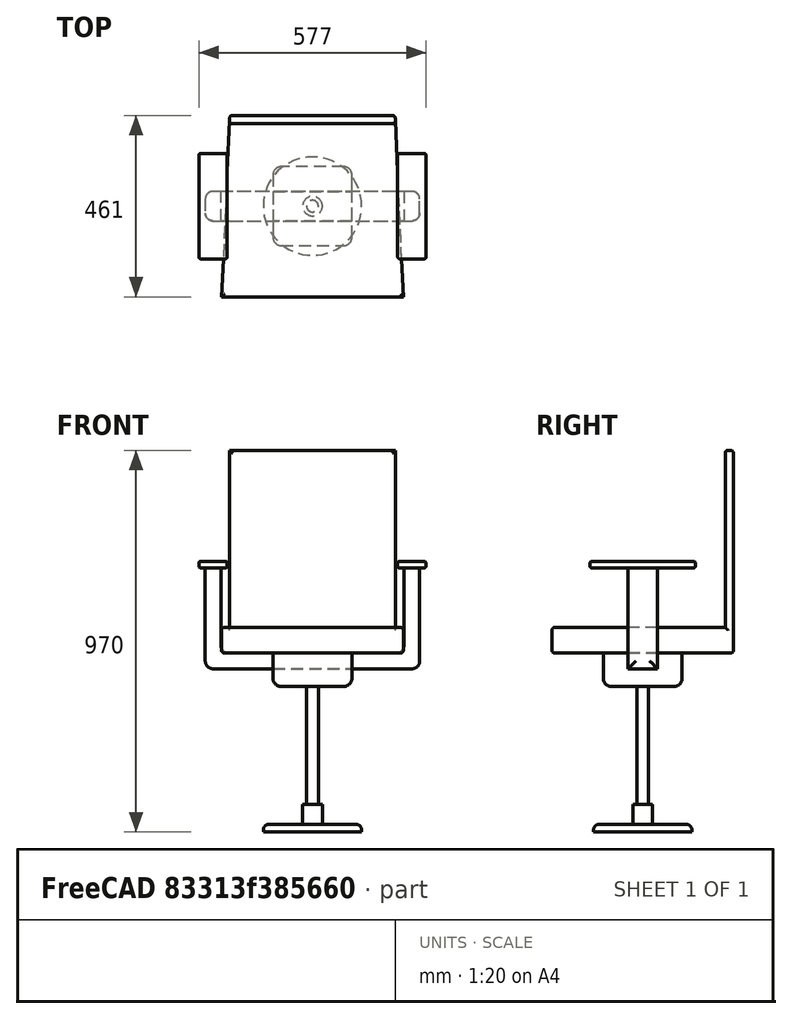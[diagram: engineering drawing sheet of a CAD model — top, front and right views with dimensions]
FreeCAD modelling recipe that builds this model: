
FCSTD DOCUMENT  (FreeCAD 1.0R39109 (Git))
Label: chair02_006
License: All rights reserved
LicenseURL: https://en.wikipedia.org/wiki/All_rights_reserved
objects: TechDraw::DrawViewBalloon×34, Sketcher::SketchObject×10, PartDesign::Pad×10, PartDesign::Fillet×7, PartDesign::Body×5, PartDesign::ShapeBinder×4, TechDraw::DrawSVGTemplate×4, TechDraw::DrawProjGroupItem×4, TechDraw::DrawPage×4, TechDraw::DrawViewDetail×3, TechDraw::DrawViewSection×2, App::Part×1
note: 80 computed .brp shape members not serialized (recipe doc carries the construction recipe); baked Part::Feature solids carry a one-line shape summary decoded from their .brp

FEATURE [Sketcher::SketchObject] Sketch
  ArcFitTolerance = 1e-06
  AttachmentSupport = -> [XY_Plane]
  FullyConstrained = true
  MakeInternals = false
  MapMode = 5
  sketch-geometry (1):
    g0: Circle CenterX=0 CenterY=0 CenterZ=0 NormalX=0 NormalY=0 NormalZ=1 AngleXU=0 Radius=125
  constraints (2):
    c: Diameter(g0) = 250
    c: Coincident(g0,g-1)
FEATURE [PartDesign::Pad] Pad
  Direction = (0,0,1)
  Length = 20
  Length2 = 10
  Profile = -> Sketch
  ReferenceAxis = -> Sketch [N_Axis]
  Refine = true
  Suppressed = false
  Type = 0
FEATURE [Sketcher::SketchObject] Sketch001
  ArcFitTolerance = 1e-06
  AttachmentSupport = -> [Pad]
  FullyConstrained = true
  MakeInternals = false
  MapMode = 5
  Placement = pos=(0,0,20) rot=(0,0,1;0rad)
  sketch-geometry (1):
    g0: Circle CenterX=0 CenterY=0 CenterZ=0 NormalX=0 NormalY=0 NormalZ=1 AngleXU=0 Radius=25
  constraints (2):
    c: Diameter(g0) = 50
    c: Coincident(g0,g-1)
FEATURE [PartDesign::Pad] Pad001
  BaseFeature = -> Pad
  Direction = (0,0,1)
  Length = 50
  Length2 = 10
  Profile = -> Sketch001
  ReferenceAxis = -> Sketch001 [N_Axis]
  Refine = true
  Suppressed = false
  Type = 0
FEATURE [PartDesign::ShapeBinder] CopyPad001  label="Body2_Sketch_P.lane"
  Placement = pos=(0,0,50) rot=(0,0,1;0rad)
  TraceSupport = false
FEATURE [Sketcher::SketchObject] Sketch002
  ArcFitTolerance = 1e-06
  AttachmentSupport = -> [CopyPad001]
  FullyConstrained = true
  MakeInternals = false
  MapMode = 5
  Placement = pos=(0,0,70) rot=(0,0,1;0rad)
  sketch-geometry (1):
    g0: Circle CenterX=0 CenterY=0 CenterZ=0 NormalX=0 NormalY=0 NormalZ=1 AngleXU=0 Radius=15
  constraints (2):
    c: Diameter(g0) = 30
    c: Coincident(g0,g-1)
FEATURE [PartDesign::Pad] Pad002
  Direction = (0,0,1)
  Length = 300
  Length2 = 10
  Placement = pos=(0,0,50) rot=(0,0,1;0rad)
  Profile = -> Sketch002
  ReferenceAxis = -> Sketch002 [N_Axis]
  Refine = true
  Suppressed = false
  Type = 0
FEATURE [PartDesign::Body] Body001  label="Body2"
  AllowCompound = false
  Group = -> [CopyPad001,Sketch002,Pad002]
  Origin = -> Origin001
  Tip = -> Pad002
FEATURE [PartDesign::ShapeBinder] CopyPad002  label="Body3_Sketch_Plane"
  Placement = pos=(0,0,300) rot=(0,0,1;0rad)
  TraceSupport = false
FEATURE [Sketcher::SketchObject] Sketch003
  ArcFitTolerance = 1e-06
  AttachmentSupport = -> [CopyPad002]
  FullyConstrained = true
  MakeInternals = false
  MapMode = 5
  Placement = pos=(0,0,370) rot=(0,0,1;0rad)
  sketch-geometry (5):
    g0: LineSegment StartX=-100 StartY=-100 StartZ=0 EndX=100 EndY=-100 EndZ=0
    g1: LineSegment StartX=100 StartY=-100 StartZ=0 EndX=100 EndY=100 EndZ=0
    g2: LineSegment StartX=100 StartY=100 StartZ=0 EndX=-100 EndY=100 EndZ=0
    g3: LineSegment StartX=-100 StartY=100 StartZ=0 EndX=-100 EndY=-100 EndZ=0
    g4: GeomPoint [constr] X=0 Y=0 Z=0
  constraints (12):
    c: Coincident(g0,g1)
    c: Coincident(g1,g2)
    c: Coincident(g2,g3)
    c: Coincident(g3,g0)
    c: Horizontal(g0)
    c: Horizontal(g2)
    c: Vertical(g1)
    c: Vertical(g3)
    c: Symmetric(g2,g0,g4)
    c: Distance(g1,g3) = 200
    c: Distance(g0,g2) = 200
    c: Coincident(g4,g-1)
FEATURE [PartDesign::Pad] Pad003
  Direction = (0,0,1)
  Length = 45
  Length2 = 10
  Placement = pos=(0,0,300) rot=(0,0,1;0rad)
  Profile = -> Sketch003
  ReferenceAxis = -> Sketch003 [N_Axis]
  Refine = true
  Suppressed = false
  Type = 0
FEATURE [PartDesign::ShapeBinder] CopyPad003  label="Body4_Sketch_Plane"
  Placement = pos=(0,0,45) rot=(0,0,1;0rad)
  TraceSupport = false
FEATURE [Sketcher::SketchObject] Sketch004
  ArcFitTolerance = 1e-06
  AttachmentSupport = -> [CopyPad003]
  FullyConstrained = true
  MakeInternals = false
  MapMode = 5
  Placement = pos=(0,0,415) rot=(0,0,1;0rad)
  sketch-geometry (5):
    g0: LineSegment StartX=-272.5 StartY=-37.5 StartZ=0 EndX=272.5 EndY=-37.5 EndZ=0
    g1: LineSegment StartX=272.5 StartY=-37.5 StartZ=0 EndX=272.5 EndY=37.5 EndZ=0
    g2: LineSegment StartX=272.5 StartY=37.5 StartZ=0 EndX=-272.5 EndY=37.5 EndZ=0
    g3: LineSegment StartX=-272.5 StartY=37.5 StartZ=0 EndX=-272.5 EndY=-37.5 EndZ=0
    g4: GeomPoint [constr] X=0 Y=0 Z=0
  constraints (12):
    c: Coincident(g0,g1)
    c: Coincident(g1,g2)
    c: Coincident(g2,g3)
    c: Coincident(g3,g0)
    c: Horizontal(g0)
    c: Horizontal(g2)
    c: Vertical(g1)
    c: Vertical(g3)
    c: Symmetric(g2,g0,g4)
    c: Distance(g1,g3) = 545
    c: Distance(g0,g2) = 75
    c: Coincident(g4,g-1)
FEATURE [PartDesign::Pad] Pad004
  Direction = (0,0,1)
  Length = 40
  Length2 = 10
  Placement = pos=(0,0,45) rot=(0,0,1;0rad)
  Profile = -> Sketch004
  ReferenceAxis = -> Sketch004 [N_Axis]
  Refine = true
  Suppressed = false
  Type = 0
FEATURE [Sketcher::SketchObject] Sketch005
  ArcFitTolerance = 1e-06
  AttachmentSupport = -> [Pad004]
  ExternalGeometry = -> [Pad004]
  FullyConstrained = true
  MakeInternals = false
  MapMode = 5
  Placement = pos=(0,0,455) rot=(0,0,1;0rad)
  sketch-geometry (8):
    g0: LineSegment StartX=-272.5 StartY=37.5 StartZ=0 EndX=-272.5 EndY=-37.5 EndZ=0
    g1: LineSegment StartX=-272.5 StartY=-37.5 StartZ=0 EndX=-232.5 EndY=-37.5 EndZ=0
    g2: LineSegment StartX=-232.5 StartY=-37.5 StartZ=0 EndX=-232.5 EndY=37.5 EndZ=0
    g3: LineSegment StartX=-232.5 StartY=37.5 StartZ=0 EndX=-272.5 EndY=37.5 EndZ=0
    g4: LineSegment StartX=272.5 StartY=37.5 StartZ=0 EndX=232.5 EndY=37.5 EndZ=0
    g5: LineSegment StartX=232.5 StartY=37.5 StartZ=0 EndX=232.5 EndY=-37.5 EndZ=0
    g6: LineSegment StartX=232.5 StartY=-37.5 StartZ=0 EndX=272.5 EndY=-37.5 EndZ=0
    g7: LineSegment StartX=272.5 StartY=-37.5 StartZ=0 EndX=272.5 EndY=37.5 EndZ=0
  constraints (22):
    c: Coincident(g0,g1)
    c: Coincident(g1,g2)
    c: Coincident(g2,g3)
    c: Coincident(g3,g0)
    c: Vertical(g0)
    c: Vertical(g2)
    c: Horizontal(g1)
    c: Horizontal(g3)
    c: Coincident(g0,g-3)
    c: PointOnObject(g1,g-4)
    c: DistanceX(g3,g3) = 40
    c: Coincident(g4,g5)
    c: Coincident(g5,g6)
    c: Coincident(g6,g7)
    c: Coincident(g7,g4)
    c: Horizontal(g4)
    c: Horizontal(g6)
    c: Vertical(g5)
    c: Vertical(g7)
    c: Coincident(g4,g-3)
    c: PointOnObject(g5,g-4)
    c: Equal(g4,g3)
FEATURE [PartDesign::Pad] Pad005
  BaseFeature = -> Pad004
  Direction = (0,0,1)
  Length = 216
  Length2 = 10
  Placement = pos=(0,0,45) rot=(0,0,1;0rad)
  Profile = -> Sketch005
  ReferenceAxis = -> Sketch005 [N_Axis]
  Refine = true
  Suppressed = false
  Type = 0
FEATURE [Sketcher::SketchObject] Sketch006
  ArcFitTolerance = 1e-06
  AttachmentSupport = -> [Pad005]
  ExternalGeometry = -> [Pad005]
  FullyConstrained = true
  MakeInternals = false
  MapMode = 5
  Placement = pos=(0,0,671) rot=(0,0,1;0rad)
  sketch-geometry (16):
    g0: LineSegment StartX=-288.5 StartY=134 StartZ=0 EndX=-288.5 EndY=-134 EndZ=0
    g1: LineSegment StartX=-288.5 StartY=-134 StartZ=0 EndX=-216.5 EndY=-134 EndZ=0
    g2: LineSegment StartX=-216.5 StartY=-134 StartZ=0 EndX=-216.5 EndY=134 EndZ=0
    g3: LineSegment StartX=-216.5 StartY=134 StartZ=0 EndX=-288.5 EndY=134 EndZ=0
    g4: LineSegment StartX=216.5 StartY=134 StartZ=0 EndX=216.5 EndY=-134 EndZ=0
    g5: LineSegment StartX=216.5 StartY=-134 StartZ=0 EndX=288.5 EndY=-134 EndZ=0
    g6: LineSegment StartX=288.5 StartY=-134 StartZ=0 EndX=288.5 EndY=134 EndZ=0
    g7: LineSegment StartX=288.5 StartY=134 StartZ=0 EndX=216.5 EndY=134 EndZ=0
    g8: LineSegment [constr] StartX=-272.5 StartY=37.5 StartZ=0 EndX=-232.5 EndY=-37.5 EndZ=0
    g9: LineSegment [constr] StartX=-252.5 StartY=0 StartZ=0 EndX=-272.5 EndY=-37.5 EndZ=0
    g10: LineSegment [constr] StartX=232.5 StartY=37.5 StartZ=0 EndX=272.5 EndY=-37.5 EndZ=0
    g11: LineSegment [constr] StartX=272.5 StartY=37.5 StartZ=0 EndX=252.5 EndY=0 EndZ=0
    g12: LineSegment [constr] StartX=-216.5 StartY=134 StartZ=0 EndX=-288.5 EndY=-134 EndZ=0
    g13: LineSegment [constr] StartX=-288.5 StartY=134 StartZ=0 EndX=-252.5 EndY=0 EndZ=0
    g14: LineSegment [constr] StartX=216.5 StartY=134 StartZ=0 EndX=288.5 EndY=-134 EndZ=0
    g15: LineSegment [constr] StartX=288.5 StartY=134 StartZ=0 EndX=252.5 EndY=0 EndZ=0
  constraints (38):
    c: Coincident(g0,g1)
    c: Coincident(g1,g2)
    c: Coincident(g2,g3)
    c: Coincident(g3,g0)
    c: Vertical(g0)
    c: Vertical(g2)
    c: Horizontal(g1)
    c: Horizontal(g3)
    c: Coincident(g4,g5)
    c: Coincident(g5,g6)
    c: Coincident(g6,g7)
    c: Coincident(g7,g4)
    c: Vertical(g4)
    c: Vertical(g6)
    c: Horizontal(g5)
    c: Horizontal(g7)
    c: Equal(g7,g3)
    c: Equal(g2,g4)
    c: DistanceX(g3,g3) = 72
    c: Coincident(g8,g-4)
    c: Coincident(g8,g-3)
    c: Coincident(g9,g-4)
    c: Coincident(g10,g-5)
    c: Coincident(g10,g-6)
    c: Coincident(g11,g-6)
    c: Symmetric(g10,g10,g11)
    c: Symmetric(g8,g8,g9)
    c: Coincident(g12,g2)
    c: Coincident(g12,g0)
    c: Coincident(g13,g0)
    c: Symmetric(g12,g12,g13)
    c: Coincident(g9,g13)
    c: Coincident(g14,g4)
    c: Coincident(g14,g5)
    c: Coincident(g15,g6)
    c: Symmetric(g14,g14,g15)
    c: Coincident(g15,g11)
    c: DistanceY(g2,g2) = 268
FEATURE [PartDesign::Pad] Pad006
  BaseFeature = -> Pad005
  Direction = (0,0,1)
  Length = 17
  Length2 = 10
  Placement = pos=(0,0,45) rot=(0,0,1;0rad)
  Profile = -> Sketch006
  ReferenceAxis = -> Sketch006 [N_Axis]
  Refine = true
  Suppressed = false
  Type = 0
FEATURE [PartDesign::ShapeBinder] CopyPad006  label="Body5_Sketch_Plane"
  Placement = pos=(0,0,45) rot=(0,0,1;0rad)
  TraceSupport = false
FEATURE [Sketcher::SketchObject] Sketch009
  ArcFitTolerance = 1e-06
  AttachmentSupport = -> [Pad003]
  ExternalGeometry = -> [Pad003]
  FullyConstrained = true
  MakeInternals = false
  MapMode = 5
  Placement = pos=(0,0,415) rot=(0,0,1;0rad)
  sketch-geometry (8):
    g0: LineSegment StartX=-100 StartY=100 StartZ=0 EndX=-100 EndY=37.5 EndZ=0
    g1: LineSegment StartX=-100 StartY=37.5 StartZ=0 EndX=100 EndY=37.5 EndZ=0
    g2: LineSegment StartX=100 StartY=37.5 StartZ=0 EndX=100 EndY=100 EndZ=0
    g3: LineSegment StartX=100 StartY=100 StartZ=0 EndX=-100 EndY=100 EndZ=0
    g4: LineSegment StartX=100 StartY=-100 StartZ=0 EndX=100 EndY=-37.5 EndZ=0
    g5: LineSegment StartX=100 StartY=-37.5 StartZ=0 EndX=-100 EndY=-37.5 EndZ=0
    g6: LineSegment StartX=-100 StartY=-37.5 StartZ=0 EndX=-100 EndY=-100 EndZ=0
    g7: LineSegment StartX=-100 StartY=-100 StartZ=0 EndX=100 EndY=-100 EndZ=0
  constraints (21):
    c: Coincident(g0,g1)
    c: Coincident(g1,g2)
    c: Coincident(g2,g3)
    c: Coincident(g3,g0)
    c: Vertical(g0)
    c: Vertical(g2)
    c: Horizontal(g1)
    c: Horizontal(g3)
    c: Coincident(g0,g-3)
    c: PointOnObject(g1,g-4)
    c: Coincident(g4,g5)
    c: Coincident(g5,g6)
    c: Coincident(g6,g7)
    c: Coincident(g7,g4)
    c: Vertical(g6)
    c: Horizontal(g5)
    c: Horizontal(g7)
    c: Coincident(g4,g-4)
    c: PointOnObject(g5,g-3)
    c: DistanceY(g4,g1) = 75
    c: Symmetric(g1,g4,g-1)
FEATURE [PartDesign::Pad] Pad009
  BaseFeature = -> Pad003
  Direction = (0,0,1)
  Length = 40
  Length2 = 10
  Placement = pos=(0,0,300) rot=(0,0,1;0rad)
  Profile = -> Sketch009
  ReferenceAxis = -> Sketch009 [N_Axis]
  Refine = true
  Suppressed = false
  Type = 0
FEATURE [PartDesign::Fillet] Fillet003
  Base = -> Pad006 [Edge43,Edge48,Edge35,Edge40,Edge39,Edge37,Edge45,Edge47,Edge34,Edge38,Edge36,Edge33,Edge24,Edge22,Edge23,Edge21,Edge29,Edge31,Edge42,Edge46,Edge44,Edge32,Edge30,Edge41]
  BaseFeature = -> Pad006
  Placement = pos=(0,0,45) rot=(0,0,1;0rad)
  Radius = 5
  Refine = true
  SupportTransform = false
  Suppressed = false
  UseAllEdges = false
FEATURE [PartDesign::Fillet] Fillet004
  Base = -> Fillet003 [Edge57,Edge58,Edge36,Edge28,Edge22,Edge29,Edge27,Edge31]
  BaseFeature = -> Fillet003
  Placement = pos=(0,0,45) rot=(0,0,1;0rad)
  Radius = 20
  Refine = true
  SupportTransform = false
  Suppressed = false
  UseAllEdges = false
FEATURE [PartDesign::Body] Body003  label="Body4"
  AllowCompound = false
  Group = -> [CopyPad003,Sketch004,Pad004,Sketch005,Pad005,Sketch006,Pad006,Fillet003,Fillet004]
  Origin = -> Origin003
  Tip = -> Fillet004
FEATURE [PartDesign::Fillet] Fillet005
  Base = -> Pad009 [Edge7,Edge5,Edge24,Edge23,Edge1,Edge2,Edge4,Edge3]
  BaseFeature = -> Pad009
  Placement = pos=(0,0,300) rot=(0,0,1;0rad)
  Radius = 20
  Refine = true
  SupportTransform = false
  Suppressed = false
  UseAllEdges = false
FEATURE [PartDesign::Body] Body002  label="Body3"
  AllowCompound = false
  Group = -> [CopyPad002,Sketch003,Pad003,Sketch009,Pad009,Fillet005]
  Origin = -> Origin002
  Tip = -> Fillet005
FEATURE [PartDesign::Fillet] Fillet006
  Base = -> Pad001 [Edge3]
  BaseFeature = -> Pad001
  Radius = 15
  Refine = true
  SupportTransform = false
  Suppressed = false
  UseAllEdges = false
FEATURE [PartDesign::Body] Body  label="Body1"
  AllowCompound = false
  Group = -> [Sketch,Pad,Sketch001,Pad001,Fillet006]
  Origin = -> Origin
  Tip = -> Fillet006
FEATURE [Sketcher::SketchObject] Sketch007
  ArcFitTolerance = 1e-06
  AttachmentSupport = -> [CopyPad006]
  FullyConstrained = true
  MakeInternals = false
  MapMode = 5
  Placement = pos=(0,0,455) rot=(0,0,1;0rad)
  sketch-geometry (8):
    g0: LineSegment StartX=-210 StartY=230.5 StartZ=0 EndX=-231 EndY=-230.5 EndZ=0
    g1: LineSegment StartX=-231 StartY=-230.5 StartZ=0 EndX=231 EndY=-230.5 EndZ=0
    g2: LineSegment StartX=231 StartY=-230.5 StartZ=0 EndX=210 EndY=230.5 EndZ=0
    g3: LineSegment StartX=210 StartY=230.5 StartZ=0 EndX=-210 EndY=230.5 EndZ=0
    g4: LineSegment [constr] StartX=210 StartY=230.5 StartZ=0 EndX=2.84e-14 EndY=0 EndZ=0
    g5: LineSegment [constr] StartX=2.84e-14 StartY=0 StartZ=0 EndX=-210 EndY=230.5 EndZ=0
    g6: LineSegment [constr] StartX=210 StartY=230.5 StartZ=0 EndX=210 EndY=0 EndZ=0
    g7: LineSegment [constr] StartX=231 StartY=-230.5 StartZ=0 EndX=231 EndY=0 EndZ=0
  constraints (20):
    c: Coincident(g2,g1)
    c: DistanceX(g1,g1) = 462
    c: DistanceX(g3,g3) = 420
    c: Coincident(g1,g0)
    c: Symmetric(g2,g0,g-2)
    c: Coincident(g2,g3)
    c: Coincident(g3,g0)
    c: Coincident(g4,g2)
    c: Coincident(g4,g-1)
    c: Coincident(g5,g4)
    c: Coincident(g5,g0)
    c: DistanceY(g2,g2) = 461
    c: Coincident(g6,g2)
    c: PointOnObject(g6,g-1)
    c: Vertical(g6)
    c: Coincident(g7,g1)
    c: PointOnObject(g7,g-1)
    c: Vertical(g7)
    c: Equal(g7,g6)
    c: Symmetric(g1,g0,g-2)
FEATURE [PartDesign::Pad] Pad007
  Direction = (0,0,1)
  Length = 65
  Length2 = 10
  Placement = pos=(0,0,45) rot=(0,0,1;0rad)
  Profile = -> Sketch007
  ReferenceAxis = -> Sketch007 [N_Axis]
  Refine = true
  Suppressed = false
  Type = 0
FEATURE [Sketcher::SketchObject] Sketch008
  ArcFitTolerance = 1e-06
  AttachmentSupport = -> [Pad007]
  ExternalGeometry = -> [Pad007]
  FullyConstrained = true
  MakeInternals = false
  MapMode = 5
  Placement = pos=(0,0,520) rot=(0,0,1;0rad)
  sketch-geometry (4):
    g0: LineSegment StartX=-210 StartY=230.5 StartZ=0 EndX=210 EndY=230.5 EndZ=0
    g1: LineSegment StartX=-210 StartY=230.5 StartZ=0 EndX=-210.957 EndY=209.5 EndZ=0
    g2: LineSegment StartX=-210.957 StartY=209.5 StartZ=0 EndX=210.957 EndY=209.5 EndZ=0
    g3: LineSegment StartX=210 StartY=230.5 StartZ=0 EndX=210.957 EndY=209.5 EndZ=0
  constraints (10):
    c: Coincident(g0,g-3)
    c: Coincident(g0,g-4)
    c: Coincident(g1,g0)
    c: PointOnObject(g1,g-3)
    c: Coincident(g2,g1)
    c: PointOnObject(g2,g-4)
    c: Horizontal(g2)
    c: Coincident(g3,g0)
    c: Coincident(g3,g2)
    c: DistanceY(g1,g1) = 21
FEATURE [PartDesign::Pad] Pad008
  BaseFeature = -> Pad007
  Direction = (0,0,1)
  Length = 450
  Length2 = 10
  Placement = pos=(0,0,45) rot=(0,0,1;0rad)
  Profile = -> Sketch008
  ReferenceAxis = -> Sketch008 [N_Axis]
  Refine = true
  Suppressed = false
  Type = 0
FEATURE [PartDesign::Fillet] Fillet
  Base = -> Pad008 [Edge13,Edge14,Edge17,Edge18,Edge12,Edge11]
  BaseFeature = -> Pad008
  Placement = pos=(0,0,45) rot=(0,0,1;0rad)
  Radius = 7
  Refine = true
  SupportTransform = false
  Suppressed = false
  UseAllEdges = false
FEATURE [PartDesign::Fillet] Fillet001
  Base = -> Fillet [Edge10,Edge17,Edge22]
  BaseFeature = -> Fillet
  Placement = pos=(0,0,45) rot=(0,0,1;0rad)
  Radius = 7
  Refine = true
  SupportTransform = false
  Suppressed = false
  UseAllEdges = false
FEATURE [PartDesign::Fillet] Fillet002
  Base = -> Fillet001 [Edge13,Edge9,Edge3,Edge12]
  BaseFeature = -> Fillet001
  Placement = pos=(0,0,45) rot=(0,0,1;0rad)
  Radius = 7
  Refine = true
  SupportTransform = false
  Suppressed = false
  UseAllEdges = false
FEATURE [PartDesign::Body] Body004  label="Body5"
  AllowCompound = false
  Group = -> [CopyPad006,Sketch007,Pad007,Sketch008,Pad008,Fillet,Fillet001,Fillet002]
  Origin = -> Origin004
  Tip = -> Fillet002
FEATURE [App::Part] Part  label="chair02"
  Group = -> [Body,Body001,Body002,Body003,Body004]
  Origin = -> Origin005
FEATURE [TechDraw::DrawSVGTemplate] Template  label="テンプレート"
  Height = 210
  Orientation = 1
  Template = <userpath>/AppData/Local/Programs/FreeCAD 1.0/data/Mod/TechDraw/Templates/A4_Landscape_blank.svg
  Width = 297
FEATURE [TechDraw::DrawProjGroupItem] View
  CoarseView = false
  Direction = (0,0,1)
  Focus = 100
  HardHidden = true
  IsoCount = 0
  IsoHidden = false
  IsoVisible = false
  LockPosition = false
  Perspective = false
  Rotation = 0
  RotationVector = (1,0,0)
  Scale = 0.333333
  ScaleType = 2
  ScrubCount = 1
  SeamHidden = false
  SeamVisible = false
  SmoothHidden = false
  SmoothVisible = true
  Source = -> [Part]
  Type = 0
  X = 148.5
  XDirection = (1,0,0)
  Y = 105
FEATURE [TechDraw::DrawViewBalloon] Balloon  label="吹き出し"
  BubbleShape = 1
  EndType = 0
  EndTypeScale = 1
  KinkLength = 5
  LockPosition = false
  OriginX = 208.147
  OriginY = 228.561
  Rotation = 0
  Scale = 0.2
  ScaleType = 2
  ShapeScale = 1
  SourceView = -> View
  Text = R7
  TextWrapLen = -1
  X = 254.043
  Y = 271.744
FEATURE [TechDraw::DrawViewBalloon] Balloon001  label="吹き出し001"
  BubbleShape = 1
  EndType = 0
  EndTypeScale = 1
  KinkLength = 5
  LockPosition = false
  OriginX = 208.8
  OriginY = 211.781
  Rotation = 0
  Scale = 0.2
  ScaleType = 2
  ShapeScale = 1
  SourceView = -> View
  Text = R7
  TextWrapLen = -1
  X = 266.359
  Y = 184.985
FEATURE [TechDraw::DrawViewBalloon] Balloon002  label="吹き出し002"
  BubbleShape = 1
  EndType = 0
  EndTypeScale = 1
  KinkLength = 5
  LockPosition = false
  OriginX = -208.147
  OriginY = 228.561
  Rotation = 0
  Scale = 0.2
  ScaleType = 2
  ShapeScale = 1
  SourceView = -> View
  Text = R7
  TextWrapLen = -1
  X = -260.711
  Y = 284.764
FEATURE [TechDraw::DrawViewBalloon] Balloon003  label="吹き出し003"
  BubbleShape = 1
  EndType = 0
  EndTypeScale = 1
  KinkLength = 5
  LockPosition = false
  OriginX = -208.439
  OriginY = 210.657
  Rotation = 0
  Scale = 0.2
  ScaleType = 2
  ShapeScale = 1
  SourceView = -> View
  Text = R7
  TextWrapLen = -1
  X = -265.342
  Y = 208.001
FEATURE [TechDraw::DrawViewBalloon] Balloon004  label="吹き出し004"
  BubbleShape = 1
  EndType = 0
  EndTypeScale = 1
  KinkLength = 5
  LockPosition = false
  OriginX = 287.036
  OriginY = 132.536
  Rotation = 0
  Scale = 0.2
  ScaleType = 2
  ShapeScale = 1
  SourceView = -> View
  Text = R5
  TextWrapLen = -1
  X = 347.036
  Y = 192.536
FEATURE [TechDraw::DrawViewBalloon] Balloon005  label="吹き出し005"
  BubbleShape = 1
  EndType = 0
  EndTypeScale = 1
  KinkLength = 5
  LockPosition = false
  OriginX = 217.209
  OriginY = 132.437
  Rotation = 0
  Scale = 0.2
  ScaleType = 2
  ShapeScale = 1
  SourceView = -> View
  Text = R5
  TextWrapLen = -1
  X = 158.961
  Y = 163.416
FEATURE [TechDraw::DrawViewBalloon] Balloon006  label="吹き出し006"
  BubbleShape = 1
  EndType = 0
  EndTypeScale = 1
  KinkLength = 5
  LockPosition = false
  OriginX = 287.036
  OriginY = -132.536
  Rotation = 0
  Scale = 0.2
  ScaleType = 2
  ShapeScale = 1
  SourceView = -> View
  Text = R5
  TextWrapLen = -1
  X = 345.184
  Y = -173.752
FEATURE [TechDraw::DrawViewBalloon] Balloon007  label="吹き出し007"
  BubbleShape = 1
  EndType = 0
  EndTypeScale = 1
  KinkLength = 5
  LockPosition = false
  OriginX = 217.101
  OriginY = -132.016
  Rotation = 0
  Scale = 0.2
  ScaleType = 2
  ShapeScale = 1
  SourceView = -> View
  Text = R5
  TextWrapLen = -1
  X = 162.924
  Y = -168.913
FEATURE [TechDraw::DrawPage] Page  label="用紙"
  KeepUpdated = true
  NextBalloonIndex = 11
  ProjectionType = 0
  Template = -> Template
  Views = -> [View,Balloon,Balloon001,Balloon002,Balloon003,Balloon004,Balloon005,Balloon006,Balloon007]
FEATURE [TechDraw::DrawSVGTemplate] Template001  label="テンプレート001"
  Height = 210
  Orientation = 1
  Template = <userpath>/AppData/Local/Programs/FreeCAD 1.0/data/Mod/TechDraw/Templates/A4_Landscape_blank.svg
  Width = 297
FEATURE [TechDraw::DrawProjGroupItem] View001
  CoarseView = false
  Direction = (0,-1,0)
  Focus = 100
  HardHidden = true
  IsoCount = 0
  IsoHidden = false
  IsoVisible = false
  LockPosition = false
  Perspective = false
  Rotation = 0
  RotationVector = (1,0,0)
  Scale = 0.2
  ScaleType = 2
  ScrubCount = 1
  SeamHidden = false
  SeamVisible = false
  SmoothHidden = false
  SmoothVisible = true
  Source = -> [Part]
  Type = 0
  X = 77.6951
  XDirection = (1,0,0)
  Y = 106.438
FEATURE [TechDraw::DrawViewDetail] Detail  label="詳細"
  AnchorPoint = (251.74,189.44,0)
  BaseView = -> View001
  CoarseView = false
  Direction = (0,-1,0)
  Focus = 100
  HardHidden = true
  IsoCount = 0
  IsoHidden = false
  IsoVisible = false
  LockPosition = false
  Perspective = false
  Radius = 39
  Reference = 1
  Rotation = 0
  Scale = 0.7
  ScaleType = 2
  ScrubCount = 1
  SeamHidden = false
  SeamVisible = false
  ShowHighlight = true
  ShowMatting = true
  SmoothHidden = false
  SmoothVisible = true
  Source = -> [Part]
  X = 198.751
  XDirection = (1,0,0)
  Y = 153.271
FEATURE [TechDraw::DrawViewDetail] Detail001  label="詳細001"
  AnchorPoint = (225.2,3.67,0)
  BaseView = -> View001
  CoarseView = false
  Direction = (0,-1,0)
  Focus = 100
  HardHidden = true
  IsoCount = 0
  IsoHidden = false
  IsoVisible = false
  LockPosition = false
  Perspective = false
  Radius = 42
  Reference = 1
  Rotation = 0
  Scale = 0.7
  ScaleType = 2
  ScrubCount = 1
  SeamHidden = false
  SeamVisible = false
  ShowHighlight = true
  ShowMatting = true
  SmoothHidden = false
  SmoothVisible = true
  Source = -> [Part]
  X = 202.09
  XDirection = (1,0,0)
  Y = 54.0888
FEATURE [TechDraw::DrawViewBalloon] Balloon008  label="吹き出し008"
  BubbleShape = 1
  EndType = 0
  EndTypeScale = 1
  KinkLength = 5
  LockPosition = false
  OriginX = 3.59213
  OriginY = 29.3328
  Rotation = 0
  Scale = 0.2
  ScaleType = 2
  ShapeScale = 1
  SourceView = -> Detail001
  Text = R7
  TextWrapLen = -1
  X = 41.6562
  Y = 43.3944
FEATURE [TechDraw::DrawViewBalloon] Balloon009  label="吹き出し009"
  BubbleShape = 1
  EndType = 0
  EndTypeScale = 1
  KinkLength = 5
  LockPosition = false
  OriginX = 3.484
  OriginY = -31.9238
  Rotation = 0
  Scale = 0.2
  ScaleType = 2
  ShapeScale = 1
  SourceView = -> Detail001
  Text = R7
  TextWrapLen = -1
  X = 41.6149
  Y = -49.4301
FEATURE [TechDraw::DrawViewBalloon] Balloon012  label="吹き出し012"
  BubbleShape = 1
  EndType = 0
  EndTypeScale = 1
  KinkLength = 5
  LockPosition = false
  OriginX = 96.5372
  OriginY = -107.388
  Rotation = 0
  Scale = 0.2
  ScaleType = 2
  ShapeScale = 1
  SourceView = -> View001
  Text = R20
  TextWrapLen = -1
  X = 176.938
  Y = -173.327
FEATURE [TechDraw::DrawViewBalloon] Balloon014  label="吹き出し014"
  BubbleShape = 1
  EndType = 0
  EndTypeScale = 1
  KinkLength = 5
  LockPosition = false
  OriginX = 114.934
  OriginY = -467.802
  Rotation = 0
  Scale = 0.2
  ScaleType = 2
  ShapeScale = 1
  SourceView = -> View001
  Text = R15
  TextWrapLen = -1
  X = 214.934
  Y = -367.802
FEATURE [TechDraw::DrawViewBalloon] Balloon016  label="吹き出し016"
  BubbleShape = 1
  EndType = 0
  EndTypeScale = 1
  KinkLength = 5
  LockPosition = false
  OriginX = 35.2955
  OriginY = 12.0955
  Rotation = 0
  Scale = 0.2
  ScaleType = 2
  ShapeScale = 1
  SourceView = -> Detail
  Text = R5
  TextWrapLen = -1
  X = 63.867
  Y = 40.847
FEATURE [TechDraw::DrawViewBalloon] Balloon017  label="吹き出し017"
  BubbleShape = 1
  EndType = 0
  EndTypeScale = 1
  KinkLength = 5
  LockPosition = false
  OriginX = 34.7958
  OriginY = -3.22508
  Rotation = 0
  Scale = 0.2
  ScaleType = 2
  ShapeScale = 1
  SourceView = -> Detail
  Text = R5
  TextWrapLen = -1
  X = 61.8285
  Y = -28.5595
FEATURE [TechDraw::DrawViewBalloon] Balloon018  label="吹き出し018"
  BubbleShape = 1
  EndType = 0
  EndTypeScale = 1
  KinkLength = 5
  LockPosition = false
  OriginX = -33.7755
  OriginY = 12.0955
  Rotation = 0
  Scale = 0.2
  ScaleType = 2
  ShapeScale = 1
  SourceView = -> Detail
  Text = R5
  TextWrapLen = -1
  X = -59.214
  Y = 35.626
FEATURE [TechDraw::DrawViewBalloon] Balloon019  label="吹き出し019"
  BubbleShape = 1
  EndType = 0
  EndTypeScale = 1
  KinkLength = 5
  LockPosition = false
  OriginX = -33.4368
  OriginY = -2.50495
  Rotation = 0
  Scale = 0.2
  ScaleType = 2
  ShapeScale = 1
  SourceView = -> Detail
  Text = R5
  TextWrapLen = -1
  X = -55.2746
  Y = -15.1611
FEATURE [TechDraw::DrawViewBalloon] Balloon020  label="吹き出し020"
  BubbleShape = 1
  EndType = 0
  EndTypeScale = 1
  KinkLength = 5
  LockPosition = false
  OriginX = 266.642
  OriginY = -64.1421
  Rotation = 0
  Scale = 0.2
  ScaleType = 2
  ShapeScale = 1
  SourceView = -> View001
  Text = R20
  TextWrapLen = -1
  X = 354.123
  Y = -146.367
FEATURE [TechDraw::DrawPage] Page001  label="用紙001"
  KeepUpdated = true
  NextBalloonIndex = 15
  ProjectionType = 0
  Template = -> Template001
  Views = -> [View001,Detail,Detail001,Balloon008,Balloon009,Balloon012,Balloon014,Balloon016,Balloon017,Balloon018,Balloon019,Balloon020]
FEATURE [TechDraw::DrawSVGTemplate] Template002  label="テンプレート002"
  Height = 210
  Orientation = 1
  Template = <userpath>/AppData/Local/Programs/FreeCAD 1.0/data/Mod/TechDraw/Templates/A4_Landscape_blank.svg
  Width = 297
FEATURE [TechDraw::DrawProjGroupItem] View002
  CoarseView = false
  Direction = (-1,-1e-16,0)
  Focus = 100
  HardHidden = true
  IsoCount = 0
  IsoHidden = false
  IsoVisible = false
  LockPosition = false
  Perspective = false
  Rotation = 0
  RotationVector = (1,0,0)
  Scale = 0.2
  ScaleType = 2
  ScrubCount = 1
  SeamHidden = false
  SeamVisible = false
  SmoothHidden = false
  SmoothVisible = true
  Source = -> [Part]
  Type = 0
  X = 89.5387
  XDirection = (1e-16,-1,0)
  Y = 105.972
FEATURE [TechDraw::DrawViewDetail] Detail002  label="詳細002"
  AnchorPoint = (127.3,193.48,0)
  BaseView = -> View002
  CoarseView = false
  Direction = (-1,-1e-16,0)
  Focus = 100
  HardHidden = true
  IsoCount = 0
  IsoHidden = false
  IsoVisible = false
  LockPosition = false
  Perspective = false
  Radius = 45
  Reference = 1
  Rotation = 0
  Scale = 0.7
  ScaleType = 2
  ScrubCount = 1
  SeamHidden = false
  SeamVisible = false
  ShowHighlight = true
  ShowMatting = true
  SmoothHidden = false
  SmoothVisible = true
  Source = -> [Part]
  X = 210.678
  XDirection = (1e-16,-1,0)
  Y = 157.676
FEATURE [TechDraw::DrawViewBalloon] Balloon021  label="吹き出し021"
  BubbleShape = 1
  EndType = 0
  EndTypeScale = 1
  KinkLength = 5
  LockPosition = false
  OriginX = 228.45
  OriginY = 32.9497
  Rotation = 0
  Scale = 0.2
  ScaleType = 2
  ShapeScale = 1
  SourceView = -> View002
  Text = R7
  TextWrapLen = -1
  X = 317.922
  Y = 84.3214
FEATURE [TechDraw::DrawViewBalloon] Balloon022  label="吹き出し022"
  BubbleShape = 1
  EndType = 0
  EndTypeScale = 1
  KinkLength = 5
  LockPosition = false
  OriginX = 229.594
  OriginY = -28.5367
  Rotation = 0
  Scale = 0.2
  ScaleType = 2
  ShapeScale = 1
  SourceView = -> View002
  Text = R7
  TextWrapLen = -1
  X = 319.567
  Y = -106.005
FEATURE [TechDraw::DrawViewBalloon] Balloon023  label="吹き出し023"
  BubbleShape = 1
  EndType = 0
  EndTypeScale = 1
  KinkLength = 5
  LockPosition = false
  OriginX = -228.45
  OriginY = -27.9497
  Rotation = 0
  Scale = 0.2
  ScaleType = 2
  ShapeScale = 1
  SourceView = -> View002
  Text = R7
  TextWrapLen = -1
  X = -300.662
  Y = -60.8802
FEATURE [TechDraw::DrawViewBalloon] Balloon024  label="吹き出し024"
  BubbleShape = 1
  EndType = 0
  EndTypeScale = 1
  KinkLength = 5
  LockPosition = false
  OriginX = -94.1421
  OriginY = -109.142
  Rotation = 0
  Scale = 0.2
  ScaleType = 2
  ShapeScale = 1
  SourceView = -> View002
  Text = R20
  TextWrapLen = -1
  X = -156.584
  Y = -142.049
FEATURE [TechDraw::DrawViewBalloon] Balloon025  label="吹き出し025"
  BubbleShape = 1
  EndType = 0
  EndTypeScale = 1
  KinkLength = 5
  LockPosition = false
  OriginX = 88.2795
  OriginY = -112.895
  Rotation = 0
  Scale = 0.2
  ScaleType = 2
  ShapeScale = 1
  SourceView = -> View002
  Text = R20
  TextWrapLen = -1
  X = 182.199
  Y = -177.075
FEATURE [TechDraw::DrawViewBalloon] Balloon026  label="吹き出し026"
  BubbleShape = 1
  EndType = 0
  EndTypeScale = 1
  KinkLength = 5
  LockPosition = false
  OriginX = 5.23553
  OriginY = 8.05553
  Rotation = 0
  Scale = 0.2
  ScaleType = 2
  ShapeScale = 1
  SourceView = -> Detail002
  Text = R5
  TextWrapLen = -1
  X = 26.0562
  Y = 24.4724
FEATURE [TechDraw::DrawViewBalloon] Balloon027  label="吹き出し027"
  BubbleShape = 1
  EndType = 0
  EndTypeScale = 1
  KinkLength = 5
  LockPosition = false
  OriginX = 5.53691
  OriginY = -6.11797
  Rotation = 0
  Scale = 0.2
  ScaleType = 2
  ShapeScale = 1
  SourceView = -> Detail002
  Text = R5
  TextWrapLen = -1
  X = 25.4768
  Y = -26.6932
FEATURE [TechDraw::DrawViewBalloon] Balloon028  label="吹き出し028"
  BubbleShape = 1
  EndType = 0
  EndTypeScale = 1
  KinkLength = 5
  LockPosition = false
  OriginX = -211.55
  OriginY = 482.95
  Rotation = 0
  Scale = 0.2
  ScaleType = 2
  ShapeScale = 1
  SourceView = -> View002
  Text = R7
  TextWrapLen = -1
  X = -135.587
  Y = 493.034
FEATURE [TechDraw::DrawViewBalloon] Balloon029  label="吹き出し029"
  BubbleShape = 1
  EndType = 0
  EndTypeScale = 1
  KinkLength = 5
  LockPosition = false
  OriginX = -229.268
  OriginY = 483.139
  Rotation = 0
  Scale = 0.2
  ScaleType = 2
  ShapeScale = 1
  SourceView = -> View002
  Text = R7
  TextWrapLen = -1
  X = -322.454
  Y = 488.771
FEATURE [TechDraw::DrawPage] Page002  label="用紙002"
  KeepUpdated = true
  NextBalloonIndex = 11
  ProjectionType = 0
  Template = -> Template002
  Views = -> [View002,Detail002,Balloon021,Balloon022,Balloon023,Balloon024,Balloon025,Balloon026,Balloon027,Balloon028,Balloon029]
FEATURE [TechDraw::DrawSVGTemplate] Template003  label="テンプレート003"
  Height = 210
  Orientation = 1
  Template = <userpath>/AppData/Local/Programs/FreeCAD 1.0/data/Mod/TechDraw/Templates/A4_Landscape_blank.svg
  Width = 297
FEATURE [TechDraw::DrawProjGroupItem] View003
  CoarseView = false
  Direction = (0,-1,0)
  Focus = 100
  HardHidden = true
  IsoCount = 0
  IsoHidden = false
  IsoVisible = false
  LockPosition = false
  Perspective = false
  Rotation = 0
  RotationVector = (1,0,0)
  Scale = 0.2
  ScaleType = 2
  ScrubCount = 1
  SeamHidden = false
  SeamVisible = false
  SmoothHidden = false
  SmoothVisible = true
  Source = -> [Part]
  Type = 0
  X = 77.0967
  XDirection = (1,0,0)
  Y = 106.651
FEATURE [TechDraw::DrawViewSection] SectionView  label="セクション  - "
  BaseView = -> View003
  CoarseView = false
  CutSurfaceDisplay = 2
  Direction = (1e-16,0,1)
  FileGeomPattern = <userpath>\AppData\Local\Programs\FreeCAD 1.0\data\Mod/TechDraw/PAT/FCPAT.pat
  FileHatchPattern = <userpath>\AppData\Local\Programs\FreeCAD 1.0\data\Mod/TechDraw/Patterns/simple.svg
  Focus = 100
  FuseBeforeCut = false
  HardHidden = true
  HatchOffset = (0,0,0)
  HatchRotation = 0
  HatchScale = 1
  IsoCount = 0
  IsoHidden = false
  IsoVisible = false
  LockPosition = false
  NameGeomPattern = Diamond
  Perspective = false
  Rotation = 0
  Scale = 0.2
  ScaleType = 2
  ScrubCount = 1
  SeamHidden = false
  SeamVisible = false
  SectionDirection = 4
  SectionLineStretch = 1
  SectionNormal = (1e-16,0,1)
  SectionOrigin = (0,0,438)
  SmoothHidden = false
  SmoothVisible = true
  Source = -> [Part]
  TrimAfterCut = false
  UsePreviousCut = false
  X = 218.379
  XDirection = (1,0,-1e-16)
  Y = 49.3365
FEATURE [TechDraw::DrawViewSection] SectionView001  label="セクション001  - "
  BaseView = -> View003
  CoarseView = false
  CutSurfaceDisplay = 2
  Direction = (1e-16,0,1)
  FileGeomPattern = <userpath>\AppData\Local\Programs\FreeCAD 1.0\data\Mod/TechDraw/PAT/FCPAT.pat
  FileHatchPattern = <userpath>\AppData\Local\Programs\FreeCAD 1.0\data\Mod/TechDraw/Patterns/simple.svg
  Focus = 100
  FuseBeforeCut = false
  HardHidden = true
  HatchOffset = (0,0,0)
  HatchRotation = 0
  HatchScale = 1
  IsoCount = 0
  IsoHidden = false
  IsoVisible = false
  LockPosition = false
  NameGeomPattern = Diamond
  Perspective = false
  Rotation = 0
  Scale = 0.2
  ScaleType = 2
  ScrubCount = 1
  SeamHidden = false
  SeamVisible = false
  SectionDirection = 4
  SectionLineStretch = 1
  SectionNormal = (1e-16,0,1)
  SectionOrigin = (0,0,572)
  SmoothHidden = false
  SmoothVisible = true
  Source = -> [Part]
  TrimAfterCut = false
  UsePreviousCut = false
  X = 221.866
  XDirection = (1,0,-1e-16)
  Y = 155.45
FEATURE [TechDraw::DrawViewBalloon] Balloon030  label="吹き出し030"
  BubbleShape = 1
  EndType = 0
  EndTypeScale = 1
  KinkLength = 5
  LockPosition = false
  OriginX = 266.642
  OriginY = 31.6421
  Rotation = 0
  Scale = 0.2
  ScaleType = 2
  ShapeScale = 1
  SourceView = -> SectionView001
  Text = R20
  TextWrapLen = -1
  X = 334.998
  Y = 96.0423
FEATURE [TechDraw::DrawViewBalloon] Balloon031  label="吹き出し031"
  BubbleShape = 1
  EndType = 0
  EndTypeScale = 1
  KinkLength = 5
  LockPosition = false
  OriginX = 267.809
  OriginY = -31.3187
  Rotation = 0
  Scale = 0.2
  ScaleType = 2
  ShapeScale = 1
  SourceView = -> SectionView001
  Text = R20
  TextWrapLen = -1
  X = 341.781
  Y = -85.5719
FEATURE [TechDraw::DrawViewBalloon] Balloon032  label="吹き出し032"
  BubbleShape = 1
  EndType = 0
  EndTypeScale = 1
  KinkLength = 5
  LockPosition = false
  OriginX = 94.1421
  OriginY = 94.1421
  Rotation = 0
  Scale = 0.2
  ScaleType = 2
  ShapeScale = 1
  SourceView = -> SectionView
  Text = R20
  TextWrapLen = -1
  X = 209.533
  Y = 135.466
FEATURE [TechDraw::DrawViewBalloon] Balloon033  label="吹き出し033"
  BubbleShape = 1
  EndType = 0
  EndTypeScale = 1
  KinkLength = 5
  LockPosition = false
  OriginX = 94.1281
  OriginY = -94.7023
  Rotation = 0
  Scale = 0.2
  ScaleType = 2
  ShapeScale = 1
  SourceView = -> SectionView
  Text = R20
  TextWrapLen = -1
  X = 181.623
  Y = -154.378
FEATURE [TechDraw::DrawViewBalloon] Balloon034  label="吹き出し034"
  BubbleShape = 1
  EndType = 0
  EndTypeScale = 1
  KinkLength = 5
  LockPosition = false
  OriginX = -266.642
  OriginY = 31.6421
  Rotation = 0
  Scale = 0.2
  ScaleType = 2
  ShapeScale = 1
  SourceView = -> SectionView001
  Text = R20
  TextWrapLen = -1
  X = -340.746
  Y = 97.9756
FEATURE [TechDraw::DrawViewBalloon] Balloon035  label="吹き出し035"
  BubbleShape = 1
  EndType = 0
  EndTypeScale = 1
  KinkLength = 5
  LockPosition = false
  OriginX = -267.188
  OriginY = -33.4582
  Rotation = 0
  Scale = 0.2
  ScaleType = 2
  ShapeScale = 1
  SourceView = -> SectionView001
  Text = R20
  TextWrapLen = -1
  X = -340.33
  Y = -99.8669
FEATURE [TechDraw::DrawViewBalloon] Balloon036  label="吹き出し036"
  BubbleShape = 1
  EndType = 0
  EndTypeScale = 1
  KinkLength = 5
  LockPosition = false
  OriginX = -94.1421
  OriginY = 94.1421
  Rotation = 0
  Scale = 0.2
  ScaleType = 2
  ShapeScale = 1
  SourceView = -> SectionView
  Text = R20
  TextWrapLen = -1
  X = -197.573
  Y = 151.62
FEATURE [TechDraw::DrawViewBalloon] Balloon037  label="吹き出し037"
  BubbleShape = 1
  EndType = 0
  EndTypeScale = 1
  KinkLength = 5
  LockPosition = false
  OriginX = -93.5878
  OriginY = -95.9218
  Rotation = 0
  Scale = 0.2
  ScaleType = 2
  ShapeScale = 1
  SourceView = -> SectionView
  Text = R20
  TextWrapLen = -1
  X = -180.589
  Y = -134.119
FEATURE [TechDraw::DrawPage] Page003  label="用紙003"
  KeepUpdated = true
  NextBalloonIndex = 9
  ProjectionType = 0
  Template = -> Template003
  Views = -> [View003,SectionView,SectionView001,Balloon030,Balloon031,Balloon032,Balloon033,Balloon034,Balloon035,Balloon036,Balloon037]
